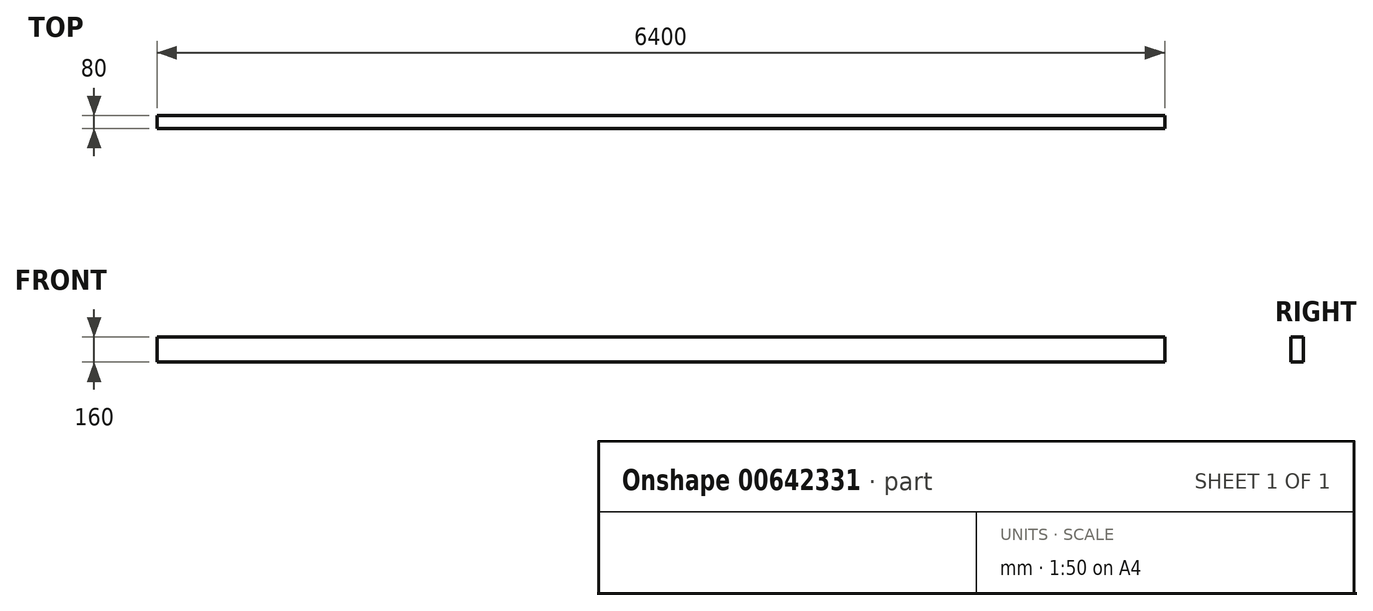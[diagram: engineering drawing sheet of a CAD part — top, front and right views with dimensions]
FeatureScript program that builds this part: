
annotation { "Feature Type Name" : "Feature", "Feature Type Description" : "" }
export const myFeature = defineFeature(function(context is Context, id is Id, definition is map)
    precondition{}
    {
        {
            var Q0;
            Q0=qCreatedBy(makeId("Right.planeOp"),FACE);
            var sketch = newSketch(context, id + "F0", { "sketchPlane" : qUnion([Q0])});
            skLineSegment(sketch, "E0.bottom", {"start": v(40, -80) * mm, "end": v(-40, -80) * mm});
            skLineSegment(sketch, "E0.top", {"start": v(40, 80) * mm, "end": v(-40, 80) * mm});
            skLineSegment(sketch, "E0.left", {"start": v(40, -80) * mm, "end": v(40, 80) * mm});
            skLineSegment(sketch, "E0.right", {"start": v(-40, -80) * mm, "end": v(-40, 80) * mm});
            skPoint(sketch, "E0.middle", {"position": v(0, 0) * mm});
            skSolve(sketch);
        }
        {
            var Q0;
            Q0=makeQuery(id+"F0.imprint","IMPRINT",FACE,{"disambiguationData":[TD([[makeQuery(id+"F0.imprint","IMPRINT",EDGE,{"derivedFrom":sQuery(id+"F0.wireOp",EDGE,"E0.bottom")}),-1.0]])]});
            extrude(context, id + "F1", {"entities" : qUnion([Q0]), "depth" : 6400 * mm, "offsetDistance" : 25 * mm});
        }
    });
